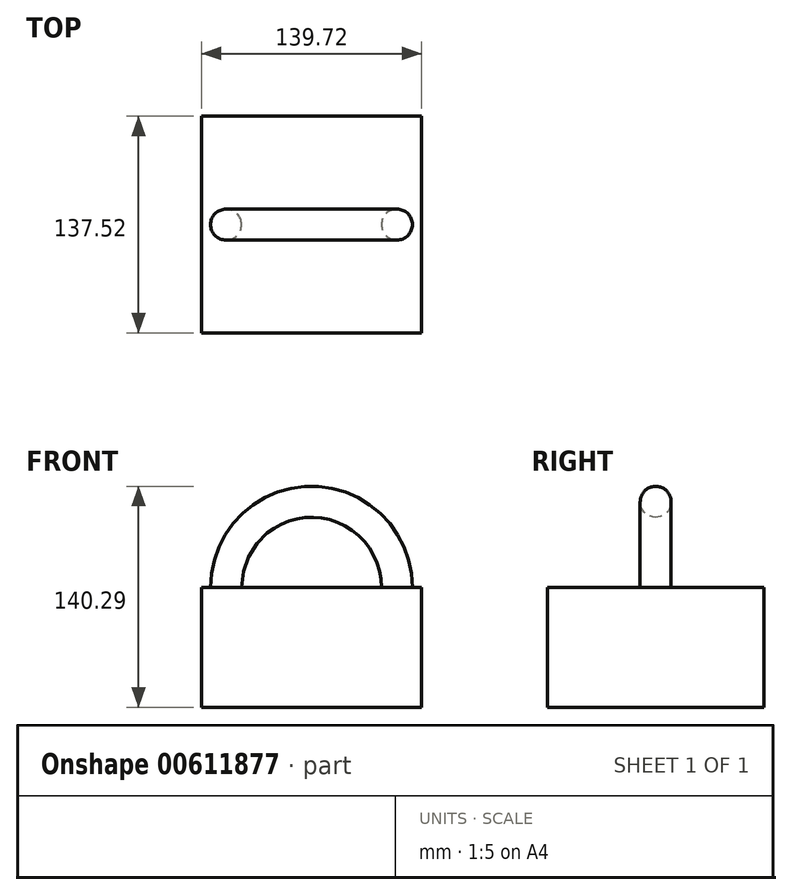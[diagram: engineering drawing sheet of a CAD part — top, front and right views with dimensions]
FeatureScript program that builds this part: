
annotation { "Feature Type Name" : "Feature", "Feature Type Description" : "" }
export const myFeature = defineFeature(function(context is Context, id is Id, definition is map)
    precondition{}
    {
        {
            var Q0;
            Q0=qCreatedBy(makeId("Top.planeOp"),FACE);
            var sketch = newSketch(context, id + "F0", { "sketchPlane" : qUnion([Q0])});
            skLineSegment(sketch, "E0.bottom", {"start": v(69.86, -68.76) * mm, "end": v(-69.86, -68.76) * mm});
            skLineSegment(sketch, "E0.top", {"start": v(69.86, 68.76) * mm, "end": v(-69.86, 68.76) * mm});
            skLineSegment(sketch, "E0.left", {"start": v(69.86, -68.76) * mm, "end": v(69.86, 68.76) * mm});
            skLineSegment(sketch, "E0.right", {"start": v(-69.86, -68.76) * mm, "end": v(-69.86, 68.76) * mm});
            skPoint(sketch, "E0.middle", {"position": v(0, 0) * mm});
            skLineSegment(sketch, "E1", {"start": v(0, 68.76) * mm, "end": v(0, -68.76) * mm});
            skSolve(sketch);
        }
        {
            var Q0;
            Q0=qCreatedBy(makeId("Top.planeOp"),FACE);
            var sketch = newSketch(context, id + "F1", { "sketchPlane" : qUnion([Q0])});
            skCircle(sketch, "E2", {"center": v(54.26, 0) * mm, "radius": 9.82 * mm});
            skSolve(sketch);
        }
        {
            var Q0;
            {var subQ0=sQuery(id+"F0.wireOp",EDGE,"E0.left");Q0=makeQuery(id+"F0.imprint","IMPRINT",FACE,{"disambiguationData":[TD([[makeQuery(id+"F0.imprint","IMPRINT",EDGE,{"derivedFrom":subQ0}),1.0]])]});}
            var Q1;
            {var subQ0=sQuery(id+"F0.wireOp",EDGE,"E0.right");Q1=makeQuery(id+"F0.imprint","IMPRINT",FACE,{"disambiguationData":[TD([[makeQuery(id+"F0.imprint","IMPRINT",EDGE,{"derivedFrom":subQ0}),-1.0]])]});}
            extrude(context, id + "F2", {"entities" : qUnion([Q0, Q1]), "oppositeDirection" : true, "depth" : 25.4 * mm, "offsetDistance" : 25.4 * mm});
        }
        {
            var Q0;
            Q0=makeQuery(id+"F2.opExtrude","CAP_FACE",FACE,{"disambiguationData":[OSD([sQuery(id+"F0.wireOp",EDGE,"E0.bottom"),sQuery(id+"F0.wireOp",EDGE,"E0.top"),sQuery(id+"F0.wireOp",EDGE,"E0.left"),sQuery(id+"F0.wireOp",EDGE,"E0.right")])],"isStart":false});
            extrude(context, id + "F3", {"entities" : qUnion([Q0]), "operationType" : NewBodyOperationType.ADD, "depth" : 25.4 * mm, "offsetDistance" : 25.4 * mm});
        }
        {
            var Q0;
            Q0=makeQuery(id+"F3.opExtrude","CAP_FACE",FACE,{"disambiguationData":[OSD([sQuery(id+"F0.wireOp",EDGE,"E0.bottom"),sQuery(id+"F0.wireOp",EDGE,"E0.top"),sQuery(id+"F0.wireOp",EDGE,"E0.left"),sQuery(id+"F0.wireOp",EDGE,"E0.right")])],"isStart":false});
            extrude(context, id + "F4", {"entities" : qUnion([Q0]), "operationType" : NewBodyOperationType.ADD, "depth" : 25.4 * mm, "offsetDistance" : 25.4 * mm});
        }
        {
            var Q0;
            Q0=makeQuery(id+"F1.imprint","IMPRINT",FACE,{"disambiguationData":[TD([[makeQuery(id+"F1.imprint","IMPRINT",EDGE,{"derivedFrom":sQuery(id+"F1.wireOp",EDGE,"E2")}),1.0]])]});
            var Q1;
            Q1=sQuery(id+"F0.wireOp",EDGE,"E1");
            revolve(context, id + "F5", {"operationType" : NewBodyOperationType.ADD, "entities" : qUnion([Q0]), "axis" : qUnion([Q1]), "revolveType" : RevolveType.FULL});
        }
    });
